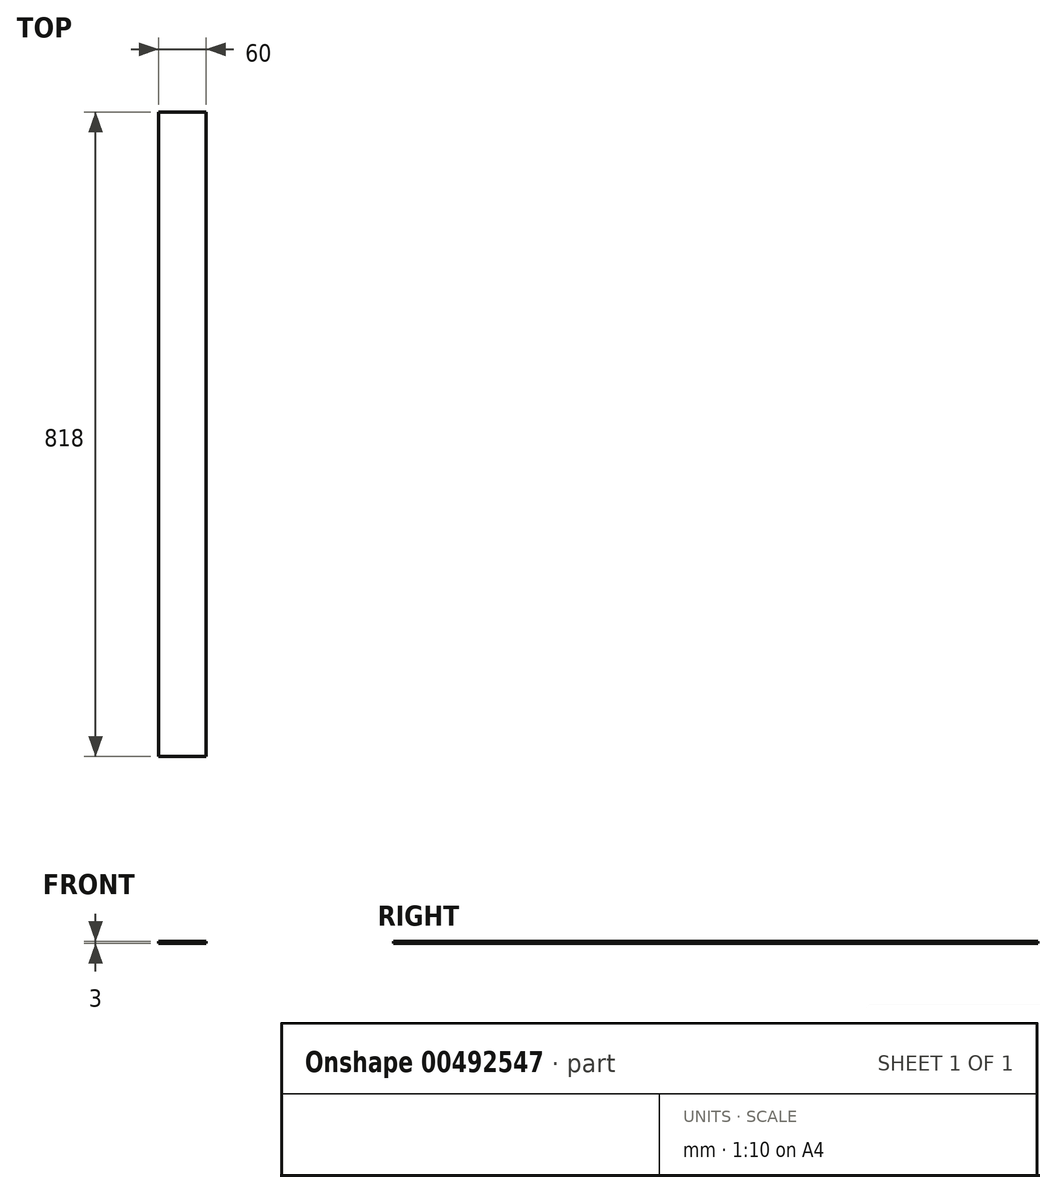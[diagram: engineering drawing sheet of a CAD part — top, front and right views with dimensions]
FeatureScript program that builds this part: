
annotation { "Feature Type Name" : "Feature", "Feature Type Description" : "" }
export const myFeature = defineFeature(function(context is Context, id is Id, definition is map)
    precondition{}
    {
        {
            var Q0;
            Q0=qCreatedBy(makeId("Top.planeOp"),FACE);
            var sketch = newSketch(context, id + "F0", { "sketchPlane" : qUnion([Q0])});
            skLineSegment(sketch, "E0.bottom", {"start": v(-40.15, 545.98) * mm, "end": v(19.85, 545.98) * mm});
            skLineSegment(sketch, "E0.top", {"start": v(-40.15, -272.02) * mm, "end": v(19.85, -272.02) * mm});
            skLineSegment(sketch, "E0.left", {"start": v(-40.15, 545.98) * mm, "end": v(-40.15, -272.02) * mm});
            skLineSegment(sketch, "E0.right", {"start": v(19.85, 545.98) * mm, "end": v(19.85, -272.02) * mm});
            skSolve(sketch);
        }
        {
            var Q0;
            Q0=makeQuery(id+"F0.imprint","IMPRINT",FACE,{"disambiguationData":[TD([[makeQuery(id+"F0.imprint","IMPRINT",EDGE,{"derivedFrom":sQuery(id+"F0.wireOp",EDGE,"E0.bottom")}),-1.0]])]});
            extrude(context, id + "F1", {"entities" : qUnion([Q0]), "depth" : 3 * mm});
        }
    });
